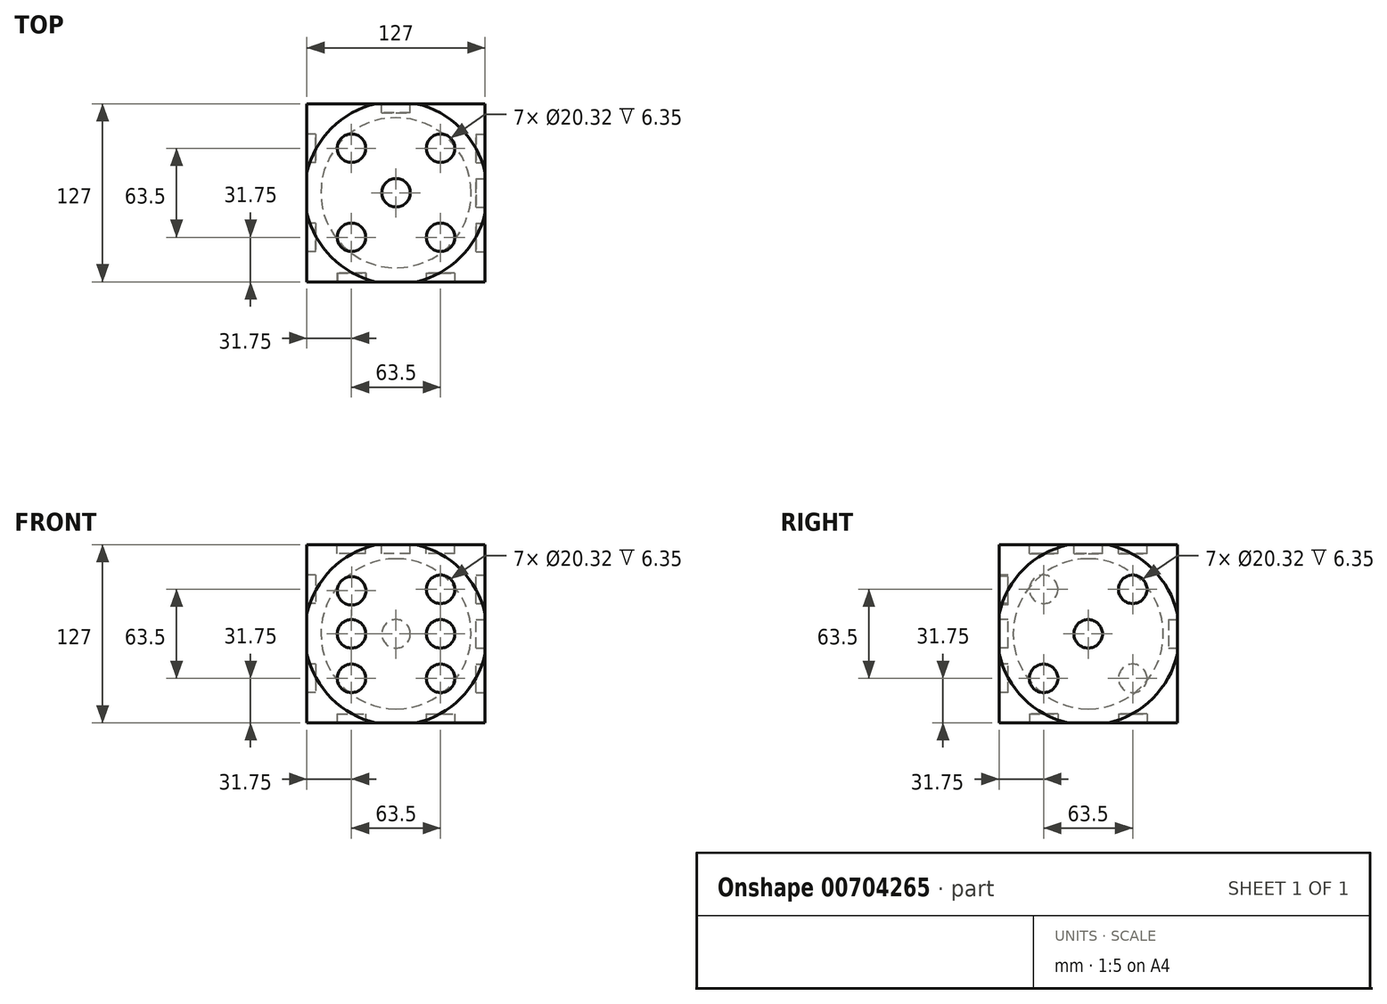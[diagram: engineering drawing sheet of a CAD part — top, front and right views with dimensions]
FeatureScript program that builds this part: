
annotation { "Feature Type Name" : "Feature", "Feature Type Description" : "" }
export const myFeature = defineFeature(function(context is Context, id is Id, definition is map)
    precondition{}
    {
        {
            var Q0;
            Q0=qCreatedBy(makeId("Top.planeOp"),FACE);
            var sketch = newSketch(context, id + "F0", { "sketchPlane" : qUnion([Q0])});
            skLineSegment(sketch, "E0.bottom", {"start": v(63.5, -63.5) * mm, "end": v(-63.5, -63.5) * mm});
            skLineSegment(sketch, "E0.top", {"start": v(63.5, 63.5) * mm, "end": v(-63.5, 63.5) * mm});
            skLineSegment(sketch, "E0.left", {"start": v(63.5, -63.5) * mm, "end": v(63.5, 63.5) * mm});
            skLineSegment(sketch, "E0.right", {"start": v(-63.5, -63.5) * mm, "end": v(-63.5, 63.5) * mm});
            skPoint(sketch, "E0.middle", {"position": v(0, 0) * mm});
            skSolve(sketch);
        }
        {
            var Q0;
            Q0=qCreatedBy(makeId("Top.planeOp"),FACE);
            cPlane(context, id + "F1", {"entities" : qUnion([Q0]), "cplaneType" : CPlaneType.OFFSET, "offset" : 63.5 * mm, "width" : 152.4 * mm, "height" : 152.4 * mm});
        }
        {
            var Q0;
            Q0=qSketchRegion(id+"F0",true);
            extrude(context, id + "F2", {"entities" : qUnion([Q0]), "depth" : 127 * mm, "offsetDistance" : 25.4 * mm});
        }
        {
            var Q0;
            Q0=qCreatedBy(id+"F1.planeOp",FACE);
            var sketch = newSketch(context, id + "F3", { "sketchPlane" : qUnion([Q0])});
            skArc(sketch, "E1", {"start": v(0, 90.94) * mm, "mid": v(-90.94, 0) * mm, "end": v(0, -90.94) * mm});
            skLineSegment(sketch, "E2", {"start": v(0, 90.94) * mm, "end": v(0, -90.94) * mm});
            skSolve(sketch);
        }
        {
            var Q0;
            Q0=qSketchRegion(id+"F3",true);
            var Q1;
            Q1=sQuery(id+"F3.wireOp",EDGE,"E2");
            revolve(context, id + "F4", {"entities" : qUnion([Q0]), "axis" : qUnion([Q1]), "revolveType" : RevolveType.FULL});
        }
        {
            var Q0;
            Q0=makeQuery(id+"F4.opRevolve","SWEPT_BODY",BODY,{"disambiguationData":[OSD([sQuery(id+"F3.wireOp",EDGE,"E1"),sQuery(id+"F3.wireOp",EDGE,"E2")])]});
            var Q1;
            Q1=makeQuery(id+"F2.opExtrude","SWEPT_BODY",BODY,{"disambiguationData":[OSD([sQuery(id+"F0.wireOp",EDGE,"E0.bottom"),sQuery(id+"F0.wireOp",EDGE,"E0.top"),sQuery(id+"F0.wireOp",EDGE,"E0.left"),sQuery(id+"F0.wireOp",EDGE,"E0.right")])]});
            booleanBodies(context, id + "F5", {"operationType" : BooleanOperationType.INTERSECTION, "tools" : qUnion([Q0, Q1])});
        }
        {
            var Q0;
            Q0=makeQuery(id+"F2.opExtrude","SWEPT_FACE",FACE,{"disambiguationData":[OSD([sQuery(id+"F0.wireOp",EDGE,"E0.top")])]});
            var sketch = newSketch(context, id + "F6", { "sketchPlane" : qUnion([Q0])});
            skCircle(sketch, "E3", {"center": v(0, 63.5) * mm, "radius": 10.16 * mm});
            skSolve(sketch);
        }
        {
            var Q0;
            Q0=makeQuery(id+"F6.imprint","IMPRINT",FACE,{"disambiguationData":[TD([[makeQuery(id+"F6.imprint","IMPRINT",EDGE,{"derivedFrom":sQuery(id+"F6.wireOp",EDGE,"E3")}),1.0]])]});
            var Q1;
            Q1=sQuery(id+"F6.wireOp",EDGE,"E3");
            extrude(context, id + "F7", {"entities" : qUnion([Q0]), "operationType" : NewBodyOperationType.REMOVE, "surfaceEntities" : qUnion([Q1]), "oppositeDirection" : true, "depth" : 6.35 * mm, "offsetDistance" : 25.4 * mm});
        }
        {
            var Q0;
            Q0=makeQuery(id+"F2.opExtrude","SWEPT_FACE",FACE,{"disambiguationData":[OSD([sQuery(id+"F0.wireOp",EDGE,"E0.bottom")])]});
            var sketch = newSketch(context, id + "F8", { "sketchPlane" : qUnion([Q0])});
            skLineSegment(sketch, "E4", {"start": v(0, 0) * mm, "end": v(0, 127) * mm, "construction": true});
            skLineSegment(sketch, "E5", {"start": v(0, 127) * mm, "end": v(0, 127) * mm});
            skLineSegment(sketch, "E6", {"start": v(-63.5, 63.5) * mm, "end": v(63.5, 63.5) * mm, "construction": true});
            skLineSegment(sketch, "E7", {"start": v(46.03, 109.53) * mm, "end": v(0, 63.5) * mm, "construction": true});
            skLineSegment(sketch, "E8", {"start": v(0, 63.5) * mm, "end": v(46.03, 17.47) * mm, "construction": true});
            skLineSegment(sketch, "E9", {"start": v(46.03, 17.47) * mm, "end": v(46.03, 17.47) * mm});
            skLineSegment(sketch, "E10", {"start": v(0, 63.5) * mm, "end": v(-46.03, 17.47) * mm, "construction": true});
            skLineSegment(sketch, "E11", {"start": v(0, 63.5) * mm, "end": v(-46.03, 109.53) * mm, "construction": true});
            skLineSegment(sketch, "E12", {"start": v(0, 63.5) * mm, "end": v(31.75, 63.5) * mm, "construction": true});
            skLineSegment(sketch, "E13", {"start": v(0, 63.5) * mm, "end": v(-31.75, 63.5) * mm, "construction": true});
            skLineSegment(sketch, "E14", {"start": v(-31.75, 63.5) * mm, "end": v(-31.75, 63.5) * mm});
            skLineSegment(sketch, "E15", {"start": v(31.75, 63.5) * mm, "end": v(31.75, 95.25) * mm, "construction": true});
            skLineSegment(sketch, "E16", {"start": v(31.75, 95.25) * mm, "end": v(31.75, 95.25) * mm});
            skLineSegment(sketch, "E17", {"start": v(31.75, 63.5) * mm, "end": v(31.75, 31.75) * mm, "construction": true});
            skLineSegment(sketch, "E18", {"start": v(-31.75, 63.5) * mm, "end": v(-31.75, 95.25) * mm, "construction": true});
            skLineSegment(sketch, "E19", {"start": v(-31.75, 63.5) * mm, "end": v(-31.75, 31.75) * mm, "construction": true});
            skCircle(sketch, "E20", {"center": v(31.75, 95.25) * mm, "radius": 10.16 * mm});
            skCircle(sketch, "E21", {"center": v(31.75, 63.5) * mm, "radius": 10.16 * mm});
            skCircle(sketch, "E22", {"center": v(31.75, 31.75) * mm, "radius": 10.16 * mm});
            skCircle(sketch, "E23", {"center": v(-31.75, 31.75) * mm, "radius": 10.16 * mm});
            skCircle(sketch, "E24", {"center": v(-31.75, 63.5) * mm, "radius": 10.16 * mm});
            skCircle(sketch, "E25", {"center": v(-31.64, 94.17) * mm, "radius": 10.16 * mm});
            skSolve(sketch);
        }
        {
            var Q0;
            Q0=qSketchRegion(id+"F8",true);
            extrude(context, id + "F9", {"entities" : qUnion([Q0]), "operationType" : NewBodyOperationType.REMOVE, "oppositeDirection" : true, "depth" : 6.35 * mm, "offsetDistance" : 25.4 * mm});
        }
        {
            var Q0;
            Q0=makeQuery(id+"F2.opExtrude","CAP_FACE",FACE,{"disambiguationData":[OSD([sQuery(id+"F0.wireOp",EDGE,"E0.bottom"),sQuery(id+"F0.wireOp",EDGE,"E0.top"),sQuery(id+"F0.wireOp",EDGE,"E0.left"),sQuery(id+"F0.wireOp",EDGE,"E0.right")])],"isStart":false});
            var sketch = newSketch(context, id + "F10", { "sketchPlane" : qUnion([Q0])});
            skLineSegment(sketch, "E26", {"start": v(0, 63.5) * mm, "end": v(0, -63.5) * mm, "construction": true});
            skLineSegment(sketch, "E27", {"start": v(0, -63.5) * mm, "end": v(0, -63.5) * mm});
            skLineSegment(sketch, "E28", {"start": v(-63.5, 0) * mm, "end": v(-31.75, 0) * mm, "construction": true});
            skLineSegment(sketch, "E29", {"start": v(63.5, 0) * mm, "end": v(63.5, 0) * mm});
            skLineSegment(sketch, "E30", {"start": v(0, 0) * mm, "end": v(46.03, 46.03) * mm, "construction": true});
            skLineSegment(sketch, "E31", {"start": v(46.03, 46.03) * mm, "end": v(46.03, 46.03) * mm});
            skLineSegment(sketch, "E32", {"start": v(0, 0) * mm, "end": v(46.03, -46.03) * mm, "construction": true});
            skLineSegment(sketch, "E33", {"start": v(0, 0) * mm, "end": v(-46.03, -46.03) * mm, "construction": true});
            skLineSegment(sketch, "E34", {"start": v(0, 0) * mm, "end": v(-46.03, 46.03) * mm, "construction": true});
            skLineSegment(sketch, "E35", {"start": v(0, 0) * mm, "end": v(-31.75, 0) * mm, "construction": true});
            skLineSegment(sketch, "E36", {"start": v(31.75, 0) * mm, "end": v(31.75, 31.75) * mm, "construction": true});
            skLineSegment(sketch, "E37", {"start": v(31.75, 31.75) * mm, "end": v(31.75, 31.75) * mm});
            skLineSegment(sketch, "E38", {"start": v(-31.75, 0) * mm, "end": v(-31.75, -31.75) * mm, "construction": true});
            skLineSegment(sketch, "E39", {"start": v(-31.75, -31.75) * mm, "end": v(-31.75, -31.75) * mm});
            skLineSegment(sketch, "E40", {"start": v(-31.75, 0) * mm, "end": v(-31.75, 31.75) * mm, "construction": true});
            skLineSegment(sketch, "E41.trimOffspring", {"start": v(0, 0) * mm, "end": v(63.5, 0) * mm, "construction": true});
            skLineSegment(sketch, "E42", {"start": v(31.75, 0) * mm, "end": v(31.75, -31.75) * mm, "construction": true});
            skCircle(sketch, "E43", {"center": v(0, 0) * mm, "radius": 10.16 * mm});
            skCircle(sketch, "E44", {"center": v(31.75, 31.75) * mm, "radius": 10.16 * mm});
            skCircle(sketch, "E45", {"center": v(31.75, -31.75) * mm, "radius": 10.16 * mm});
            skCircle(sketch, "E46", {"center": v(-31.75, -31.75) * mm, "radius": 10.16 * mm});
            skCircle(sketch, "E47", {"center": v(-31.75, 31.75) * mm, "radius": 10.16 * mm});
            skSolve(sketch);
        }
        {
            var Q0;
            Q0=qSketchRegion(id+"F10",true);
            extrude(context, id + "F11", {"entities" : qUnion([Q0]), "operationType" : NewBodyOperationType.REMOVE, "oppositeDirection" : true, "depth" : 6.35 * mm, "offsetDistance" : 25.4 * mm});
        }
        {
            var Q0;
            Q0=makeQuery(id+"F2.opExtrude","CAP_FACE",FACE,{"disambiguationData":[OSD([sQuery(id+"F0.wireOp",EDGE,"E0.bottom"),sQuery(id+"F0.wireOp",EDGE,"E0.top"),sQuery(id+"F0.wireOp",EDGE,"E0.left"),sQuery(id+"F0.wireOp",EDGE,"E0.right")])],"isStart":true});
            var sketch = newSketch(context, id + "F12", { "sketchPlane" : qUnion([Q0])});
            skLineSegment(sketch, "E48", {"start": v(0, 0) * mm, "end": v(63.5, 0) * mm, "construction": true});
            skLineSegment(sketch, "E49", {"start": v(63.5, 0) * mm, "end": v(63.5, 0) * mm});
            skLineSegment(sketch, "E50", {"start": v(0, 0) * mm, "end": v(-63.5, 0) * mm});
            skLineSegment(sketch, "E51", {"start": v(-63.5, 0) * mm, "end": v(0, 0) * mm, "construction": true});
            skLineSegment(sketch, "E52", {"start": v(0, 0) * mm, "end": v(-46.03, -46.03) * mm, "construction": true});
            skLineSegment(sketch, "E53", {"start": v(-46.03, -46.03) * mm, "end": v(-46.03, -46.03) * mm});
            skLineSegment(sketch, "E54", {"start": v(0, 0) * mm, "end": v(46.03, 46.03) * mm, "construction": true});
            skLineSegment(sketch, "E55", {"start": v(46.03, 46.03) * mm, "end": v(46.03, 46.03) * mm});
            skLineSegment(sketch, "E56", {"start": v(31.75, 0) * mm, "end": v(31.75, 31.75) * mm, "construction": true});
            skPoint(sketch, "E56.endSnap0", {"position": v(31.75, 0) * mm});
            skLineSegment(sketch, "E57", {"start": v(-31.75, 0) * mm, "end": v(-31.75, -31.75) * mm, "construction": true});
            skCircle(sketch, "E58", {"center": v(31.75, 31.75) * mm, "radius": 10.16 * mm});
            skCircle(sketch, "E59", {"center": v(-31.75, -31.75) * mm, "radius": 10.16 * mm});
            skSolve(sketch);
        }
        {
            var Q0;
            Q0=qSketchRegion(id+"F12",true);
            extrude(context, id + "F13", {"entities" : qUnion([Q0]), "operationType" : NewBodyOperationType.REMOVE, "oppositeDirection" : true, "depth" : 6.35 * mm, "offsetDistance" : 25.4 * mm});
        }
        {
            var Q0;
            Q0=makeQuery(id+"F2.opExtrude","SWEPT_FACE",FACE,{"disambiguationData":[OSD([sQuery(id+"F0.wireOp",EDGE,"E0.left")])]});
            var sketch = newSketch(context, id + "F14", { "sketchPlane" : qUnion([Q0])});
            skLineSegment(sketch, "E60", {"start": v(0, 63.5) * mm, "end": v(63.5, 63.5) * mm, "construction": true});
            skLineSegment(sketch, "E61", {"start": v(0, 63.5) * mm, "end": v(-63.5, 63.5) * mm, "construction": true});
            skLineSegment(sketch, "E62", {"start": v(0, 63.5) * mm, "end": v(46.03, 109.53) * mm, "construction": true});
            skLineSegment(sketch, "E63", {"start": v(0, 63.5) * mm, "end": v(-46.03, 17.47) * mm, "construction": true});
            skLineSegment(sketch, "E64", {"start": v(-46.03, 17.47) * mm, "end": v(-46.03, 17.47) * mm});
            skLineSegment(sketch, "E65", {"start": v(31.75, 63.5) * mm, "end": v(31.75, 95.25) * mm});
            skLineSegment(sketch, "E66", {"start": v(-31.75, 63.5) * mm, "end": v(-31.75, 31.75) * mm});
            skCircle(sketch, "E67", {"center": v(0, 63.5) * mm, "radius": 10.16 * mm});
            skCircle(sketch, "E68", {"center": v(31.75, 95.25) * mm, "radius": 10.16 * mm});
            skCircle(sketch, "E69", {"center": v(-31.75, 31.75) * mm, "radius": 10.16 * mm});
            skSolve(sketch);
        }
        {
            var Q0;
            Q0=qSketchRegion(id+"F14",true);
            extrude(context, id + "F15", {"entities" : qUnion([Q0]), "operationType" : NewBodyOperationType.REMOVE, "oppositeDirection" : true, "depth" : 6.35 * mm, "offsetDistance" : 25.4 * mm});
        }
        {
            var Q0;
            Q0=makeQuery(id+"F2.opExtrude","SWEPT_FACE",FACE,{"disambiguationData":[OSD([sQuery(id+"F0.wireOp",EDGE,"E0.right")])]});
            var sketch = newSketch(context, id + "F16", { "sketchPlane" : qUnion([Q0])});
            skLineSegment(sketch, "E70", {"start": v(0, 63.5) * mm, "end": v(63.5, 63.5) * mm, "construction": true});
            skLineSegment(sketch, "E71", {"start": v(63.5, 63.5) * mm, "end": v(63.5, 63.5) * mm});
            skLineSegment(sketch, "E72", {"start": v(0, 63.5) * mm, "end": v(-63.5, 63.5) * mm, "construction": true});
            skLineSegment(sketch, "E73", {"start": v(0, 63.5) * mm, "end": v(46.03, 109.53) * mm, "construction": true});
            skLineSegment(sketch, "E74", {"start": v(0, 63.5) * mm, "end": v(-46.03, 17.47) * mm, "construction": true});
            skLineSegment(sketch, "E75", {"start": v(-31.75, 63.5) * mm, "end": v(-31.75, 31.75) * mm, "construction": true});
            skLineSegment(sketch, "E76", {"start": v(-31.75, 31.75) * mm, "end": v(-31.75, 31.75) * mm});
            skLineSegment(sketch, "E77", {"start": v(0, 63.5) * mm, "end": v(-46.03, 109.53) * mm, "construction": true});
            skLineSegment(sketch, "E78", {"start": v(-46.03, 109.53) * mm, "end": v(-46.03, 109.53) * mm});
            skLineSegment(sketch, "E79", {"start": v(0, 63.5) * mm, "end": v(46.03, 17.47) * mm, "construction": true});
            skLineSegment(sketch, "E80", {"start": v(-31.75, 63.5) * mm, "end": v(-31.75, 95.25) * mm, "construction": true});
            skLineSegment(sketch, "E81", {"start": v(31.75, 63.5) * mm, "end": v(31.75, 95.25) * mm, "construction": true});
            skLineSegment(sketch, "E82", {"start": v(31.75, 63.5) * mm, "end": v(31.75, 31.75) * mm, "construction": true});
            skCircle(sketch, "E83", {"center": v(-31.75, 95.25) * mm, "radius": 10.16 * mm});
            skCircle(sketch, "E84", {"center": v(-31.75, 31.75) * mm, "radius": 10.16 * mm});
            skCircle(sketch, "E85", {"center": v(31.75, 31.75) * mm, "radius": 10.16 * mm});
            skCircle(sketch, "E86", {"center": v(31.75, 95.25) * mm, "radius": 10.16 * mm});
            skSolve(sketch);
        }
        {
            var Q0;
            Q0=qSketchRegion(id+"F16",true);
            extrude(context, id + "F17", {"entities" : qUnion([Q0]), "operationType" : NewBodyOperationType.REMOVE, "oppositeDirection" : true, "depth" : 6.35 * mm, "offsetDistance" : 25.4 * mm});
        }
        {
            var Q0;
            Q0=qCreatedBy(makeId("Front.planeOp"),FACE);
            var sketch = newSketch(context, id + "F18", { "sketchPlane" : qUnion([Q0])});
            skArc(sketch, "E87", {"start": v(0, 117) * mm, "mid": v(-53.5, 63.5) * mm, "end": v(0, 10) * mm});
            skLineSegment(sketch, "E88", {"start": v(0, 117) * mm, "end": v(0, 10) * mm});
            skSolve(sketch);
        }
        {
            var Q0;
            Q0=qCreatedBy(makeId("Front.planeOp"),FACE);
            var sketch = newSketch(context, id + "F19", { "sketchPlane" : qUnion([Q0])});
            skLineSegment(sketch, "E89", {"start": v(0, 0) * mm, "end": v(0, -32.49) * mm});
            skSolve(sketch);
        }
        {
            var Q0;
            Q0=makeQuery(id+"F18.imprint","IMPRINT",FACE,{"disambiguationData":[TD([[makeQuery(id+"F18.imprint","IMPRINT",EDGE,{"derivedFrom":sQuery(id+"F18.wireOp",EDGE,"E87")}),1.0]])]});
            var Q1;
            Q1=sQuery(id+"F19.wireOp",EDGE,"E89");
            revolve(context, id + "F20", {"entities" : qUnion([Q0]), "axis" : qUnion([Q1]), "revolveType" : RevolveType.FULL});
        }
        {
            var Q0;
            Q0=makeQuery(id+"F20.opRevolve","SWEPT_BODY",BODY,{"disambiguationData":[OSD([sQuery(id+"F18.wireOp",EDGE,"E87"),sQuery(id+"F18.wireOp",EDGE,"E88")])]});
            var Q1;
            Q1=makeQuery(id+"F5.opBoolean","INTERSECT",BODY,{"derivedFrom":[makeQuery(id+"F2.opExtrude","SWEPT_BODY",BODY,{"disambiguationData":[OSD([sQuery(id+"F0.wireOp",EDGE,"E0.bottom"),sQuery(id+"F0.wireOp",EDGE,"E0.top"),sQuery(id+"F0.wireOp",EDGE,"E0.left"),sQuery(id+"F0.wireOp",EDGE,"E0.right")])]}),makeQuery(id+"F4.opRevolve","SWEPT_BODY",BODY,{"disambiguationData":[OSD([sQuery(id+"F3.wireOp",EDGE,"E1"),sQuery(id+"F3.wireOp",EDGE,"E2")])]})]});
            booleanBodies(context, id + "F21", {"operationType" : BooleanOperationType.SUBTRACTION, "tools" : qUnion([Q0]), "targets" : qUnion([Q1])});
        }
    });
